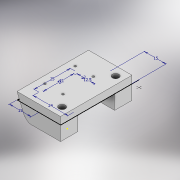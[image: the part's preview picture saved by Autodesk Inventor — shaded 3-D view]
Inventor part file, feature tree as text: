
AUTODESK INVENTOR PART (.ipt)
format: ipt  version: 2021 (Build 250183000, 183)  size: 165,888 bytes
history: native  units: mm
features: sketch x2, extrude x2, hole x2, chamfer x2, fillet x1
ambient origin geometry x8: Origin, YZ Plane, XZ Plane, XY Plane, X Axis, Y Axis, Z Axis, Center Point
bodies: Solid1 (feature_tree)
feature tree (9):
  sketch  "Sketch1"  dims[d0=15.0mm d5=15.0mm]
  extrude  "Extrusion1"  Depth=15.0mm
  hole  "Hole1"  [1 undecoded]
  extrude  "Extrusion2"  Depth=4.0mm
  hole  "Hole2"  [1 undecoded]
  chamfer  "Chamfer1"  Distance=2.0mm
  chamfer  "Chamfer2"  Distance=2.0mm
  fillet  "Fillet1"  Radius=5.0mm
  sketch  "Sketch2"  dims[d8=24.0mm d9=25.0mm d14=12.5mm d15=21.0mm d16=2.0mm d17=2.0mm d18=5.0mm d19=0.0mm d20=1.5mm d21=6.0mm d22=4.0mm d23=2.0mm d24=90.0deg d25=8.0mm d26=20.594885mm d27=30.0mm d28=12.0mm d29=30.0mm d30=12.0mm d31=10.0mm d32=0.0mm d33=4.5mm d34=6.0mm d35=4.0mm d36=2.0mm d37=90.0deg d38=8.0mm d39=20.594885mm d40=8.0mm d41=2.0mm d42=45.0deg d43=7.0mm d44=2.0mm d45=45.0deg d46=4.0mm]
note: 2 required parameter values undecoded (feature->parameter linkage not recoverable at this tier; creation-order binding heuristic only, values carry confidence <= 0.55)
